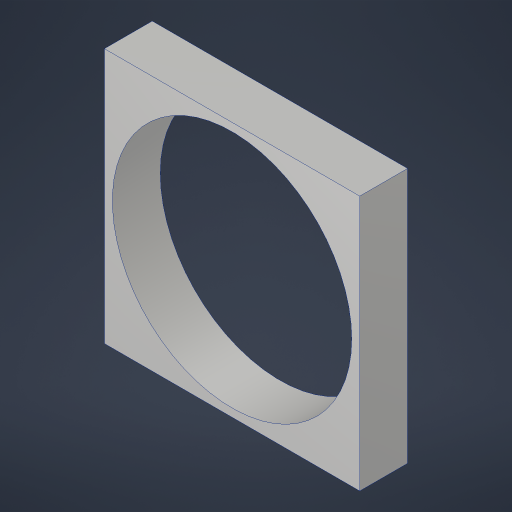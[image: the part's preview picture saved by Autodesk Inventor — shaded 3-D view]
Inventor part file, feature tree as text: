
AUTODESK INVENTOR PART (.ipt)
format: ipt  version: 2023.4 (Build 274418000, 418)  size: 178,176 bytes
history: native  units: in
note: dims shown in document units (in); Inventor stores cm internally (conversion verified against a paired STEP export)
features: extrude x2, sketch x1
ambient origin geometry x8: Origin, YZ Plane, XZ Plane, XY Plane, X Axis, Y Axis, Z Axis, Center Point
bodies: Solid1 (feature_tree)
feature tree (3):
  extrude  "Extrusion1"  Depth=1.875in
  extrude  "Extrusion2"  TaperAngle=0.0deg  [1 undecoded]
  sketch  "Sketch2"  dims[d3=0.0in d4=1.875in d5=0.0in d6=0.0in]
note: 1 required parameter value undecoded (feature->parameter linkage not recoverable at this tier; creation-order binding heuristic only, values carry confidence <= 0.55)
